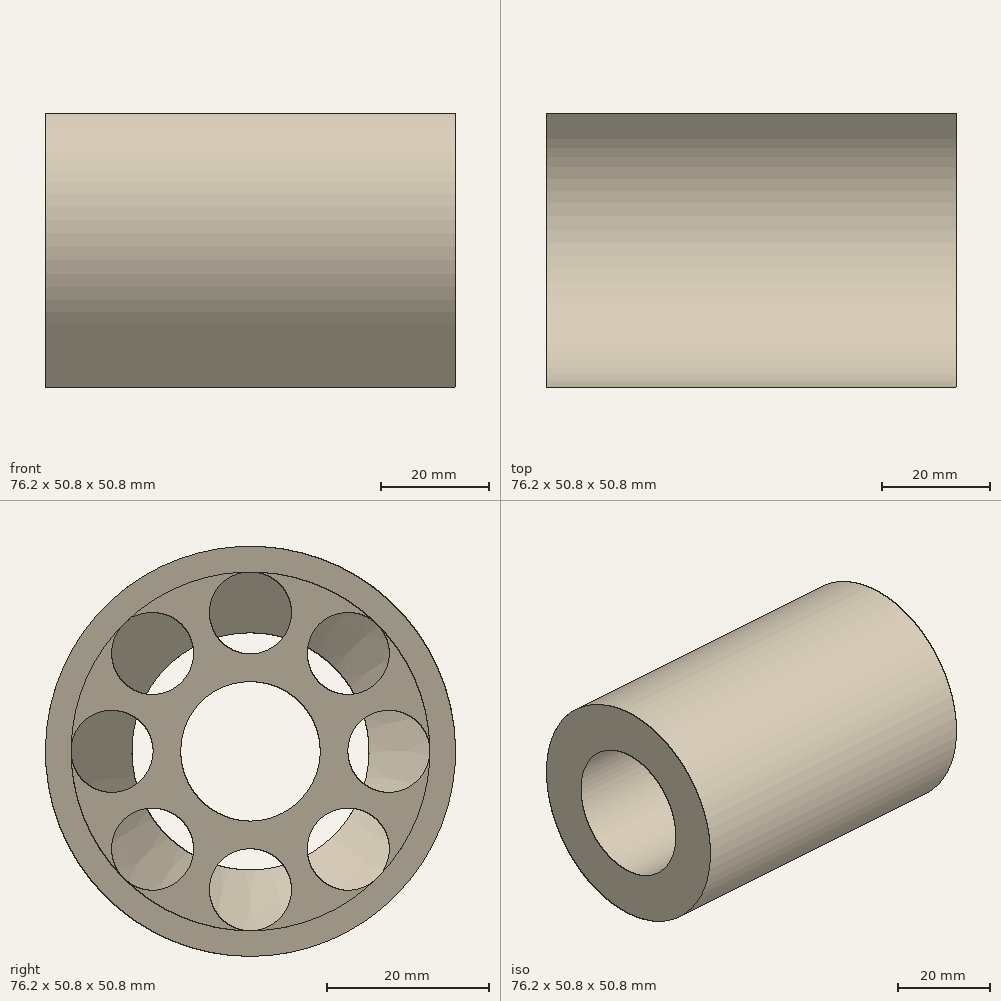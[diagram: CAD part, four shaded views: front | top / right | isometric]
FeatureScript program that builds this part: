
annotation { "Feature Type Name" : "Feature", "Feature Type Description" : "" }
export const myFeature = defineFeature(function(context is Context, id is Id, definition is map)
    precondition{}
    {
        {
            var Q0;
            Q0=qCreatedBy(makeId("Right.planeOp"),FACE);
            var sketch = newSketch(context, id + "F0", { "sketchPlane" : qUnion([Q0])});
            skCircle(sketch, "E0", {"center": v(0, 0) * mm, "radius": 25.4 * mm});
            skSolve(sketch);
        }
        {
            var Q0;
            Q0=makeQuery(id+"F0.imprint","IMPRINT",FACE,{"disambiguationData":[TD([[makeQuery(id+"F0.imprint","IMPRINT",EDGE,{"derivedFrom":sQuery(id+"F0.wireOp",EDGE,"E0")}),1.0]])]});
            extrude(context, id + "F1", {"entities" : qUnion([Q0]), "endBound" : BoundingType.SYMMETRIC, "depth" : 76.2 * mm});
        }
        {
            var Q0;
            Q0=makeQuery(id+"F1.opExtrude","CAP_FACE",FACE,{"disambiguationData":[OSD([sQuery(id+"F0.wireOp",EDGE,"E0")])],"isStart":false});
            var sketch = newSketch(context, id + "F2", { "sketchPlane" : qUnion([Q0])});
            skCircle(sketch, "E1", {"center": v(0, 0) * mm, "radius": 22.23 * mm});
            skSolve(sketch);
        }
        {
            var Q0;
            Q0=makeQuery(id+"F2.imprint","IMPRINT",FACE,{"disambiguationData":[TD([[makeQuery(id+"F2.imprint","IMPRINT",EDGE,{"derivedFrom":sQuery(id+"F2.wireOp",EDGE,"E1")}),1.0]])]});
            extrude(context, id + "F3", {"entities" : qUnion([Q0]), "operationType" : NewBodyOperationType.REMOVE, "oppositeDirection" : true, "depth" : 33.7 * mm});
        }
        {
            var Q0;
            Q0=makeQuery(id+"F3.boolean.opBoolean","COPY",FACE,{"derivedFrom":makeQuery(id+"F3.opExtrude","CAP_FACE",FACE,{"disambiguationData":[OSD([sQuery(id+"F2.wireOp",EDGE,"E1")])],"isStart":false})});
            var sketch = newSketch(context, id + "F4", { "sketchPlane" : qUnion([Q0])});
            skCircle(sketch, "E2", {"center": v(0, 0) * mm, "radius": 17.14 * mm, "construction": true});
            skCircle(sketch, "E3", {"center": v(0, 17.14) * mm, "radius": 5.08 * mm});
            skCircle(sketch, "E4", {"center": v(12.12, 12.12) * mm, "radius": 5.08 * mm});
            skCircle(sketch, "E5", {"center": v(17.14, 0) * mm, "radius": 5.08 * mm});
            skCircle(sketch, "E6", {"center": v(0, -17.14) * mm, "radius": 5.08 * mm});
            skCircle(sketch, "E7", {"center": v(-17.14, 0) * mm, "radius": 5.08 * mm});
            skCircle(sketch, "E8", {"center": v(-12.12, 12.12) * mm, "radius": 5.08 * mm});
            skCircle(sketch, "E9", {"center": v(-12.12, -12.12) * mm, "radius": 5.08 * mm});
            skCircle(sketch, "E10", {"center": v(12.12, -12.12) * mm, "radius": 5.08 * mm});
            skLineSegment(sketch, "E11", {"start": v(-12.12, -12.12) * mm, "end": v(12.12, 12.12) * mm, "construction": true});
            skLineSegment(sketch, "E12", {"start": v(-12.12, 12.12) * mm, "end": v(12.12, -12.12) * mm, "construction": true});
            skCircle(sketch, "E13", {"center": v(0, 0) * mm, "radius": 8.64 * mm});
            skSolve(sketch);
        }
        {
            var Q0;
            Q0=makeQuery(id+"F4.imprint","IMPRINT",FACE,{"disambiguationData":[TD([[makeQuery(id+"F4.imprint","IMPRINT",EDGE,{"derivedFrom":sQuery(id+"F4.wireOp",EDGE,"E8")}),1.0]])]});
            var Q1;
            Q1=makeQuery(id+"F4.imprint","IMPRINT",FACE,{"disambiguationData":[TD([[makeQuery(id+"F4.imprint","IMPRINT",EDGE,{"derivedFrom":sQuery(id+"F4.wireOp",EDGE,"E7")}),1.0]])]});
            var Q2;
            Q2=makeQuery(id+"F4.imprint","IMPRINT",FACE,{"disambiguationData":[TD([[makeQuery(id+"F4.imprint","IMPRINT",EDGE,{"derivedFrom":sQuery(id+"F4.wireOp",EDGE,"E9")}),1.0]])]});
            var Q3;
            Q3=makeQuery(id+"F4.imprint","IMPRINT",FACE,{"disambiguationData":[TD([[makeQuery(id+"F4.imprint","IMPRINT",EDGE,{"derivedFrom":sQuery(id+"F4.wireOp",EDGE,"E6")}),1.0]])]});
            var Q4;
            Q4=makeQuery(id+"F4.imprint","IMPRINT",FACE,{"disambiguationData":[TD([[makeQuery(id+"F4.imprint","IMPRINT",EDGE,{"derivedFrom":sQuery(id+"F4.wireOp",EDGE,"E10")}),1.0]])]});
            var Q5;
            Q5=makeQuery(id+"F4.imprint","IMPRINT",FACE,{"disambiguationData":[TD([[makeQuery(id+"F4.imprint","IMPRINT",EDGE,{"derivedFrom":sQuery(id+"F4.wireOp",EDGE,"E5")}),1.0]])]});
            var Q6;
            Q6=makeQuery(id+"F4.imprint","IMPRINT",FACE,{"disambiguationData":[TD([[makeQuery(id+"F4.imprint","IMPRINT",EDGE,{"derivedFrom":sQuery(id+"F4.wireOp",EDGE,"E4")}),1.0]])]});
            var Q7;
            Q7=makeQuery(id+"F4.imprint","IMPRINT",FACE,{"disambiguationData":[TD([[makeQuery(id+"F4.imprint","IMPRINT",EDGE,{"derivedFrom":sQuery(id+"F4.wireOp",EDGE,"E3")}),1.0]])]});
            var Q8;
            Q8=makeQuery(id+"F4.imprint","IMPRINT",FACE,{"disambiguationData":[TD([[makeQuery(id+"F4.imprint","IMPRINT",EDGE,{"derivedFrom":sQuery(id+"F4.wireOp",EDGE,"E13")}),1.0]])]});
            extrude(context, id + "F5", {"entities" : qUnion([Q0, Q1, Q2, Q3, Q4, Q5, Q6, Q7, Q8]), "operationType" : NewBodyOperationType.REMOVE, "oppositeDirection" : true, "depth" : 9.52 * mm});
        }
        {
            var Q0;
            Q0=qCreatedBy(makeId("Top.planeOp"),FACE);
            var sketch = newSketch(context, id + "F6", { "sketchPlane" : qUnion([Q0])});
            skLineSegment(sketch, "E14.0", {"start": v(-5.13, 22.23) * mm, "end": v(-5.13, 12.06) * mm, "construction": true});
            skLineSegment(sketch, "E15", {"start": v(-5.13, 22.23) * mm, "end": v(-12.67, 14.68) * mm});
            skLineSegment(sketch, "E16", {"start": v(-12.67, 14.68) * mm, "end": v(-38.1, 14.68) * mm});
            skLineSegment(sketch, "E17", {"start": v(-5.13, 22.23) * mm, "end": v(0, 22.23) * mm});
            skLineSegment(sketch, "E18", {"start": v(0, 22.23) * mm, "end": v(0, 0) * mm});
            skLineSegment(sketch, "E19", {"start": v(0, 0) * mm, "end": v(-38.1, 0) * mm});
            skLineSegment(sketch, "E20", {"start": v(-38.1, 0) * mm, "end": v(-38.1, 14.68) * mm});
            skSolve(sketch);
        }
        {
            var Q0;
            Q0 = qSketchRegion(id + "F6", true);
            var Q1;
            Q1=makeQuery(id+"F1.opExtrude","SWEPT_FACE",FACE,{"disambiguationData":[OSD([sQuery(id+"F0.wireOp",EDGE,"E0")])]});
            revolve(context, id + "F7", {"operationType" : NewBodyOperationType.REMOVE, "entities" : qUnion([Q0]), "axis" : qUnion([Q1]), "revolveType" : RevolveType.FULL, "oppositeDirection" : true});
        }
    });
